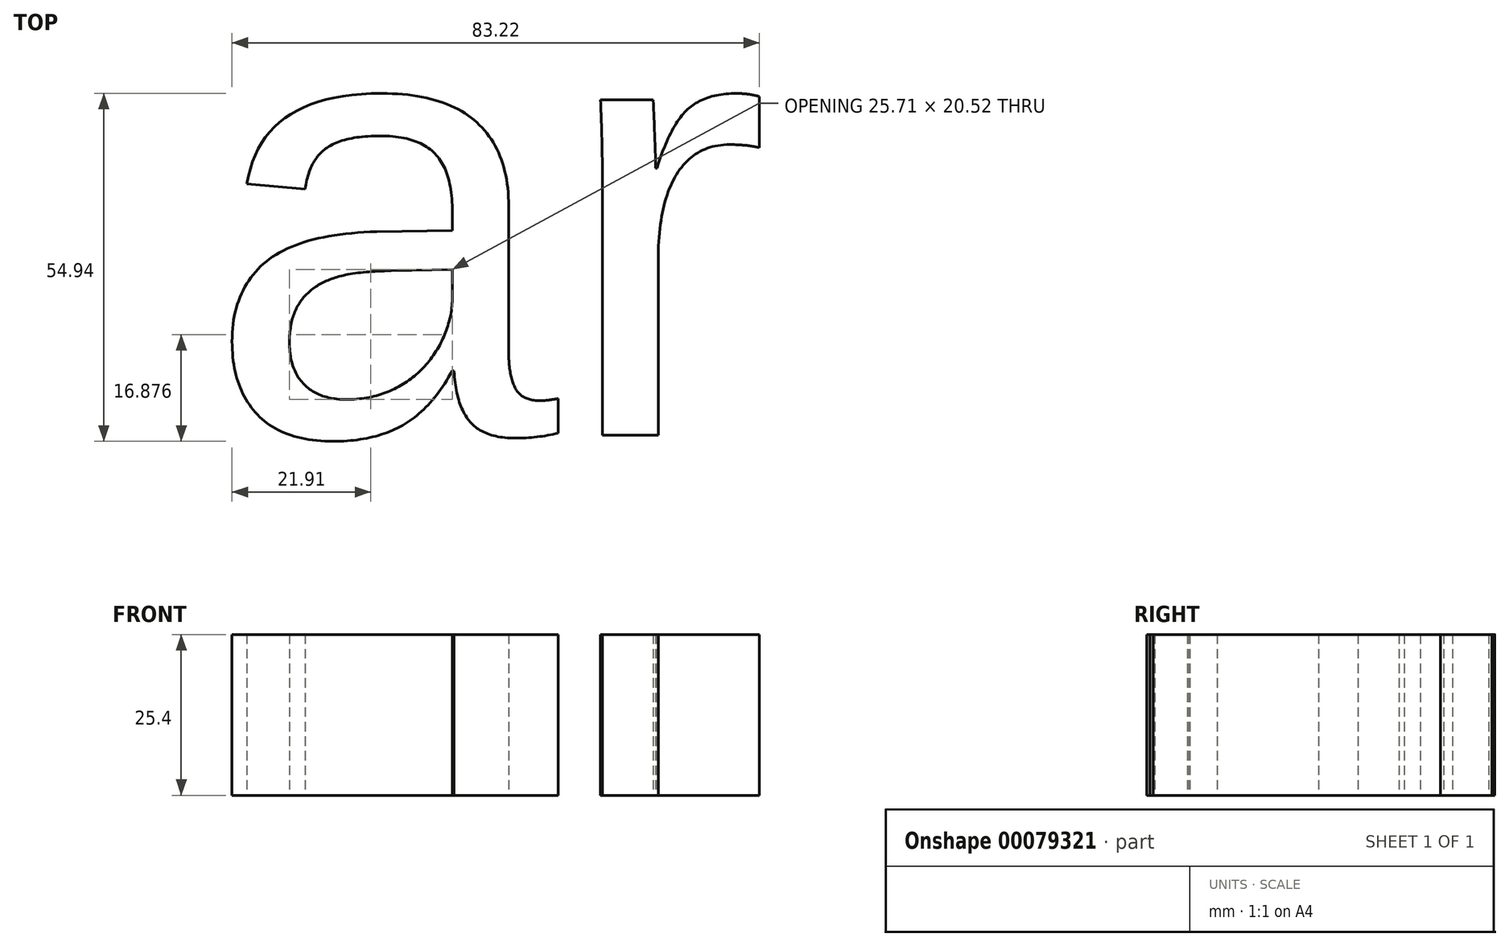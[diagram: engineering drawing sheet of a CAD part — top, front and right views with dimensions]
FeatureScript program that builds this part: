
annotation { "Feature Type Name" : "Feature", "Feature Type Description" : "" }
export const myFeature = defineFeature(function(context is Context, id is Id, definition is map)
    precondition{}
    {
        {
            var Q0;
            Q0=qCreatedBy(makeId("Top.planeOp"),FACE);
            var sketch = newSketch(context, id + "F0", { "sketchPlane" : qUnion([Q0])});
            skText(sketch, "E0", { "text": "arimo", "fontName": "Arimo-Regular.ttf"});
            const initialGuessF0  = {"E0": [-0.03141, -0.02124, 1, 0, 0.07219]};
            skSetInitialGuess(sketch, initialGuessF0);
            skSolve(sketch);
        }
        {
            var Q0;
            Q0=makeQuery(id+"F0.imprint","IMPRINT",FACE,{"disambiguationData":[TD([[makeQuery(id+"F0.imprint","IMPRINT",EDGE,{"derivedFrom":sQuery(id+"F0.wireOp",EDGE,"E0.sketch_text.stroke-35")}),-1.0]])]});
            var Q1;
            Q1=makeQuery(id+"F0.imprint","IMPRINT",FACE,{"disambiguationData":[TD([[makeQuery(id+"F0.imprint","IMPRINT",EDGE,{"derivedFrom":sQuery(id+"F0.wireOp",EDGE,"E0.sketch_text.stroke-0")}),-1.0]])]});
            extrude(context, id + "F1", {"entities" : qUnion([Q0, Q1]), "depth" : 25.4 * mm});
        }
    });
